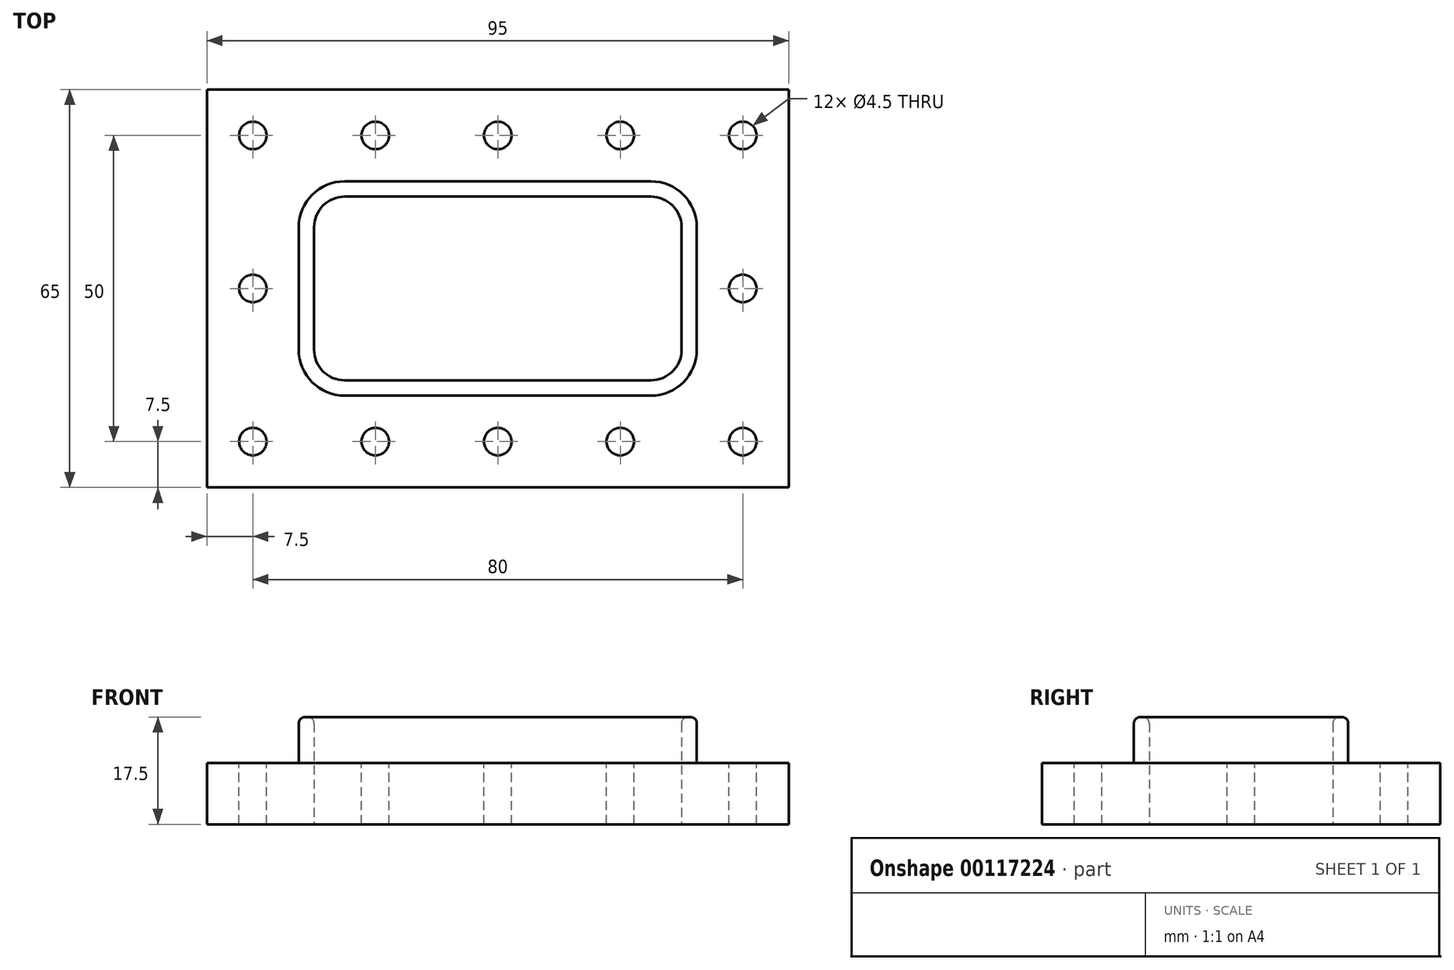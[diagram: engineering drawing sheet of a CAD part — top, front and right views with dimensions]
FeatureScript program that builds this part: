
annotation { "Feature Type Name" : "Feature", "Feature Type Description" : "" }
export const myFeature = defineFeature(function(context is Context, id is Id, definition is map)
    precondition{}
    {
        {
            var Q0;
            Q0=qCreatedBy(makeId("Top.planeOp"),FACE);
            var sketch = newSketch(context, id + "F0", { "sketchPlane" : qUnion([Q0])});
            skLineSegment(sketch, "E0.bottom", {"start": v(47.5, -32.5) * mm, "end": v(-47.5, -32.5) * mm});
            skLineSegment(sketch, "E0.top", {"start": v(47.5, 32.5) * mm, "end": v(-47.5, 32.5) * mm});
            skLineSegment(sketch, "E0.left", {"start": v(47.5, -32.5) * mm, "end": v(47.5, 32.5) * mm});
            skLineSegment(sketch, "E0.right", {"start": v(-47.5, -32.5) * mm, "end": v(-47.5, 32.5) * mm});
            skPoint(sketch, "E0.middle", {"position": v(0, 0) * mm});
            skSolve(sketch);
        }
        {
            var Q0;
            Q0=makeQuery(id+"F0.imprint","IMPRINT",FACE,{"disambiguationData":[TD([[makeQuery(id+"F0.imprint","IMPRINT",EDGE,{"derivedFrom":sQuery(id+"F0.wireOp",EDGE,"E0.bottom")}),-1.0]])]});
            extrude(context, id + "F1", {"entities" : qUnion([Q0]), "depth" : 10 * mm});
        }
        {
            var Q0;
            Q0=makeQuery(id+"F1.opExtrude","CAP_FACE",FACE,{"disambiguationData":[OSD([sQuery(id+"F0.wireOp",EDGE,"E0.bottom"),sQuery(id+"F0.wireOp",EDGE,"E0.top"),sQuery(id+"F0.wireOp",EDGE,"E0.left"),sQuery(id+"F0.wireOp",EDGE,"E0.right")])],"isStart":false});
            var sketch = newSketch(context, id + "F2", { "sketchPlane" : qUnion([Q0])});
            skLineSegment(sketch, "E1.bottom", {"start": v(25, -15) * mm, "end": v(-25, -15) * mm});
            skLineSegment(sketch, "E1.top", {"start": v(25, 15) * mm, "end": v(-25, 15) * mm});
            skLineSegment(sketch, "E1.left", {"start": v(30, -10) * mm, "end": v(30, 10) * mm});
            skLineSegment(sketch, "E1.right", {"start": v(-30, -10) * mm, "end": v(-30, 10) * mm});
            skPoint(sketch, "E1.middle", {"position": v(0, 0) * mm});
            skPoint(sketch, "E2.visualSharp", {"position": v(-30, 15) * mm});
            skArc(sketch, "E2.filletArc", {"start": v(-25, 15) * mm, "mid": v(-28.54, 13.54) * mm, "end": v(-30, 10) * mm});
            skPoint(sketch, "E3.visualSharp", {"position": v(-30, -15) * mm});
            skArc(sketch, "E3.filletArc", {"start": v(-30, -10) * mm, "mid": v(-28.54, -13.54) * mm, "end": v(-25, -15) * mm});
            skPoint(sketch, "E4.visualSharp", {"position": v(30, -15) * mm});
            skArc(sketch, "E4.filletArc", {"start": v(25, -15) * mm, "mid": v(28.54, -13.54) * mm, "end": v(30, -10) * mm});
            skPoint(sketch, "E5.visualSharp", {"position": v(30, 15) * mm});
            skArc(sketch, "E5.filletArc", {"start": v(30, 10) * mm, "mid": v(28.54, 13.54) * mm, "end": v(25, 15) * mm});
            skArc(sketch, "E6.0", {"start": v(32.5, 10) * mm, "mid": v(30.3, 15.3) * mm, "end": v(25, 17.5) * mm});
            skLineSegment(sketch, "E6.1", {"start": v(32.5, -10) * mm, "end": v(32.5, 10) * mm});
            skLineSegment(sketch, "E6.2", {"start": v(25, 17.5) * mm, "end": v(-25, 17.5) * mm});
            skArc(sketch, "E6.3", {"start": v(25, -17.5) * mm, "mid": v(30.3, -15.3) * mm, "end": v(32.5, -10) * mm});
            skArc(sketch, "E6.4", {"start": v(-25, 17.5) * mm, "mid": v(-30.3, 15.3) * mm, "end": v(-32.5, 10) * mm});
            skLineSegment(sketch, "E6.5", {"start": v(-32.5, -10) * mm, "end": v(-32.5, 10) * mm});
            skArc(sketch, "E6.6", {"start": v(-32.5, -10) * mm, "mid": v(-30.3, -15.3) * mm, "end": v(-25, -17.5) * mm});
            skLineSegment(sketch, "E6.7", {"start": v(25, -17.5) * mm, "end": v(-25, -17.5) * mm});
            skLineSegment(sketch, "E7.0", {"start": v(-42.5, -27.5) * mm, "end": v(42.5, -27.5) * mm});
            skLineSegment(sketch, "E7.1", {"start": v(-42.5, 27.5) * mm, "end": v(-42.5, -27.5) * mm});
            skLineSegment(sketch, "E7.2", {"start": v(42.5, 27.5) * mm, "end": v(-42.5, 27.5) * mm});
            skLineSegment(sketch, "E7.3", {"start": v(42.5, -27.5) * mm, "end": v(42.5, 27.5) * mm});
            skSolve(sketch);
        }
        {
            var Q0;
            Q0=makeQuery(id+"F2.imprint","IMPRINT",FACE,{"disambiguationData":[TD([[makeQuery(id+"F2.imprint","IMPRINT",EDGE,{"derivedFrom":sQuery(id+"F2.wireOp",EDGE,"E1.bottom")}),1.0]])]});
            extrude(context, id + "F3", {"entities" : qUnion([Q0]), "operationType" : NewBodyOperationType.ADD, "depth" : 7.5 * mm});
        }
        {
            var Q0;
            Q0=makeQuery(id+"F3.opExtrude","CAP_FACE",FACE,{"disambiguationData":[OSD([sQuery(id+"F2.wireOp",EDGE,"E1.bottom"),sQuery(id+"F2.wireOp",EDGE,"E1.top"),sQuery(id+"F2.wireOp",EDGE,"E1.left"),sQuery(id+"F2.wireOp",EDGE,"E1.right"),sQuery(id+"F2.wireOp",EDGE,"E2.filletArc"),sQuery(id+"F2.wireOp",EDGE,"E3.filletArc"),sQuery(id+"F2.wireOp",EDGE,"E4.filletArc"),sQuery(id+"F2.wireOp",EDGE,"E5.filletArc"),sQuery(id+"F2.wireOp",EDGE,"E6.0"),sQuery(id+"F2.wireOp",EDGE,"E6.1"),sQuery(id+"F2.wireOp",EDGE,"E6.2"),sQuery(id+"F2.wireOp",EDGE,"E6.3"),sQuery(id+"F2.wireOp",EDGE,"E6.4"),sQuery(id+"F2.wireOp",EDGE,"E6.5"),sQuery(id+"F2.wireOp",EDGE,"E6.6"),sQuery(id+"F2.wireOp",EDGE,"E6.7")])],"isStart":false});
            fillet(context, id + "F4", {"entities" : qUnion([Q0]), "radius" : 1 * mm, "tangentPropagation" : true, "allowEdgeOverflow" : false});
        }
        {
            var Q0;
            Q0=makeQuery(id+"F3.boolean.opBoolean","SPLIT",FACE,{"disambiguationData":[TD([makeQuery(id+"F3.opExtrude","SWEPT_FACE",FACE,{"disambiguationData":[OSD([sQuery(id+"F2.wireOp",EDGE,"E1.bottom")])]})])],"derivedFrom":makeQuery(id+"F1.opExtrude","CAP_FACE",FACE,{"disambiguationData":[OSD([sQuery(id+"F0.wireOp",EDGE,"E0.bottom"),sQuery(id+"F0.wireOp",EDGE,"E0.top"),sQuery(id+"F0.wireOp",EDGE,"E0.left"),sQuery(id+"F0.wireOp",EDGE,"E0.right")])],"isStart":false})});
            var sketch = newSketch(context, id + "F5", { "sketchPlane" : qUnion([Q0])});
            skLineSegment(sketch, "E8.bottom", {"start": v(25, -15) * mm, "end": v(-25, -15) * mm});
            skLineSegment(sketch, "E8.top", {"start": v(25, 15) * mm, "end": v(-25, 15) * mm});
            skLineSegment(sketch, "E8.left", {"start": v(30, -10) * mm, "end": v(30, 10) * mm});
            skLineSegment(sketch, "E8.right", {"start": v(-30, -10) * mm, "end": v(-30, 10) * mm});
            skPoint(sketch, "E8.middle", {"position": v(0, 0) * mm});
            skPoint(sketch, "E9.visualSharp", {"position": v(-30, 15) * mm});
            skArc(sketch, "E9.filletArc", {"start": v(-25, 15) * mm, "mid": v(-28.54, 13.54) * mm, "end": v(-30, 10) * mm});
            skPoint(sketch, "E10.visualSharp", {"position": v(-30, -15) * mm});
            skArc(sketch, "E10.filletArc", {"start": v(-30, -10) * mm, "mid": v(-28.54, -13.54) * mm, "end": v(-25, -15) * mm});
            skPoint(sketch, "E11.visualSharp", {"position": v(30, -15) * mm});
            skArc(sketch, "E11.filletArc", {"start": v(25, -15) * mm, "mid": v(28.54, -13.54) * mm, "end": v(30, -10) * mm});
            skPoint(sketch, "E12.visualSharp", {"position": v(30, 15) * mm});
            skArc(sketch, "E12.filletArc", {"start": v(30, 10) * mm, "mid": v(28.54, 13.54) * mm, "end": v(25, 15) * mm});
            skSolve(sketch);
        }
        {
            var Q0;
            Q0=makeQuery(id+"F5.imprint","IMPRINT",FACE,{"disambiguationData":[TD([[makeQuery(id+"F5.imprint","IMPRINT",EDGE,{"derivedFrom":sQuery(id+"F5.wireOp",EDGE,"E8.bottom")}),-1.0]])]});
            extrude(context, id + "F6", {"entities" : qUnion([Q0]), "operationType" : NewBodyOperationType.REMOVE, "endBound" : BoundingType.THROUGH_ALL, "oppositeDirection" : true, "depth" : 25 * mm});
        }
        {
            var Q0;
            {var subQ0=sQuery(id+"F0.wireOp",EDGE,"E0.bottom");var subQ1=sQuery(id+"F0.wireOp",EDGE,"E0.top");var subQ2=sQuery(id+"F0.wireOp",EDGE,"E0.left");var subQ3=sQuery(id+"F0.wireOp",EDGE,"E0.right");Q0=makeQuery(id+"F3.boolean.opBoolean","SPLIT",FACE,{"disambiguationData":[TD([makeQuery(id+"F1.opExtrude","SWEPT_FACE",FACE,{"disambiguationData":[OSD([subQ0])]})])],"derivedFrom":makeQuery(id+"F1.opExtrude","CAP_FACE",FACE,{"disambiguationData":[OSD([subQ0,subQ1,subQ2,subQ3])],"isStart":false})});}
            var sketch = newSketch(context, id + "F7", { "sketchPlane" : qUnion([Q0])});
            skLineSegment(sketch, "E13.bottom", {"start": v(40, -25) * mm, "end": v(-40, -25) * mm, "construction": true});
            skLineSegment(sketch, "E13.top", {"start": v(40, 25) * mm, "end": v(-40, 25) * mm, "construction": true});
            skLineSegment(sketch, "E13.left", {"start": v(40, -25) * mm, "end": v(40, 25) * mm, "construction": true});
            skLineSegment(sketch, "E13.right", {"start": v(-40, -25) * mm, "end": v(-40, 25) * mm, "construction": true});
            skPoint(sketch, "E13.middle", {"position": v(0, 0) * mm});
            skCircle(sketch, "E14", {"center": v(-40, 25) * mm, "radius": 2.25 * mm});
            skCircle(sketch, "E15.0.1.0", {"center": v(-40, 0) * mm, "radius": 2.25 * mm});
            skCircle(sketch, "E15.0.2.0", {"center": v(-40, -25) * mm, "radius": 2.25 * mm});
            skCircle(sketch, "E15.1.0.0", {"center": v(-20, 25) * mm, "radius": 2.25 * mm});
            skCircle(sketch, "E15.1.2.0", {"center": v(-20, -25) * mm, "radius": 2.25 * mm});
            skCircle(sketch, "E15.2.0.0", {"center": v(0, 25) * mm, "radius": 2.25 * mm});
            skCircle(sketch, "E15.2.2.0", {"center": v(0, -25) * mm, "radius": 2.25 * mm});
            skCircle(sketch, "E15.3.0.0", {"center": v(20, 25) * mm, "radius": 2.25 * mm});
            skCircle(sketch, "E15.3.2.0", {"center": v(20, -25) * mm, "radius": 2.25 * mm});
            skCircle(sketch, "E15.4.0.0", {"center": v(40, 25) * mm, "radius": 2.25 * mm});
            skCircle(sketch, "E15.4.1.0", {"center": v(40, 0) * mm, "radius": 2.25 * mm});
            skCircle(sketch, "E15.4.2.0", {"center": v(40, -25) * mm, "radius": 2.25 * mm});
            skLineSegment(sketch, "E15.direction1", {"start": v(-40, 25) * mm, "end": v(-20, 25) * mm, "construction": true});
            skLineSegment(sketch, "E15.direction2", {"start": v(-40, 25) * mm, "end": v(-40, 0) * mm, "construction": true});
            skSolve(sketch);
        }
        {
            var Q0;
            Q0 = qSketchRegion(id + "F7", true);
            extrude(context, id + "F8", {"entities" : qUnion([Q0]), "operationType" : NewBodyOperationType.REMOVE, "endBound" : BoundingType.THROUGH_ALL, "oppositeDirection" : true, "depth" : 25 * mm});
        }
    });
